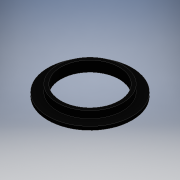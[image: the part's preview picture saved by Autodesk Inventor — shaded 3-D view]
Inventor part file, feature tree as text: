
AUTODESK INVENTOR PART (.ipt)
format: ipt  version: 2016 (Build 200138000, 138)  size: 105,984 bytes
history: native  units: mm
features: extrude x2, other x1, sketch x1
ambient origin geometry x8: Origin, YZ Plane, XZ Plane, XY Plane, X Axis, Y Axis, Z Axis, Center Point
bodies: Body1 (feature_tree)
feature tree (4):
  other  "ソリッド1"
  sketch  "スケッチ1"
  extrude  "押し出し1"  Depth=25.0mm
  extrude  "押し出し2"  Depth=28.0mm
